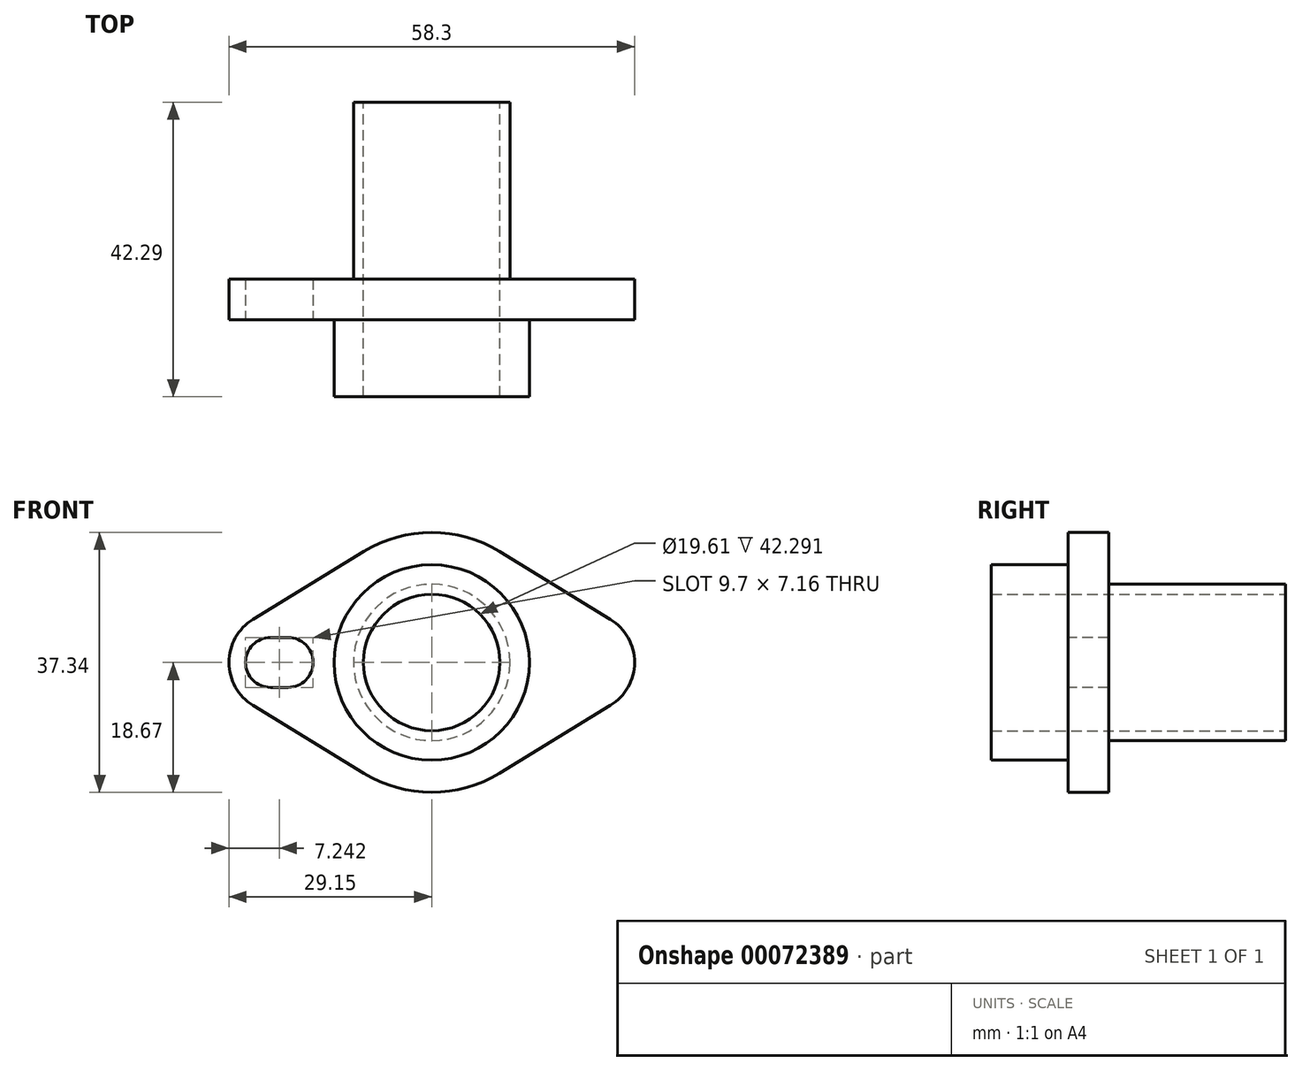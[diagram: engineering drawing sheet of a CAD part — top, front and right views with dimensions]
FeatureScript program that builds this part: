
annotation { "Feature Type Name" : "Feature", "Feature Type Description" : "" }
export const myFeature = defineFeature(function(context is Context, id is Id, definition is map)
    precondition{}
    {
        {
            var Q0;
            Q0=qCreatedBy(makeId("Front.planeOp"),FACE);
            var sketch = newSketch(context, id + "F0", { "sketchPlane" : qUnion([Q0])});
            skCircle(sketch, "E0", {"center": v(0, 0) * mm, "radius": 9.8 * mm});
            skArc(sketch, "E1", {"start": v(9.74, 15.93) * mm, "mid": v(0, 18.67) * mm, "end": v(-9.74, 15.93) * mm});
            skArc(sketch, "E2", {"start": v(25.68, -6.18) * mm, "mid": v(29.15, 0) * mm, "end": v(25.68, 6.18) * mm});
            skLineSegment(sketch, "E3", {"start": v(9.74, 15.93) * mm, "end": v(25.68, 6.18) * mm});
            skLineSegment(sketch, "E4", {"start": v(9.74, -15.93) * mm, "end": v(25.68, -6.18) * mm});
            skLineSegment(sketch, "E5.MirrorCS", {"start": v(-9.74, 15.93) * mm, "end": v(-25.68, 6.18) * mm});
            skLineSegment(sketch, "E6.MirrorCS", {"start": v(-9.74, -15.93) * mm, "end": v(-25.68, -6.18) * mm});
            skArc(sketch, "E7.MirrorCS", {"start": v(-25.68, -6.18) * mm, "mid": v(-29.15, 0) * mm, "end": v(-25.68, 6.18) * mm});
            skArc(sketch, "E8.trimOffspring", {"start": v(-9.74, -15.93) * mm, "mid": v(0, -18.67) * mm, "end": v(9.74, -15.93) * mm});
            skSolve(sketch);
        }
        {
            var Q0;
            Q0 = qSketchRegion(id + "F0", true);
            extrude(context, id + "F1", {"entities" : qUnion([Q0]), "depth" : 5.84 * mm});
        }
        {
            var Q0;
            Q0=makeQuery(id+"F1.opExtrude","CAP_FACE",FACE,{"disambiguationData":[OSD([sQuery(id+"F0.wireOp",EDGE,"E0"),sQuery(id+"F0.wireOp",EDGE,"E1"),sQuery(id+"F0.wireOp",EDGE,"E2"),sQuery(id+"F0.wireOp",EDGE,"E3"),sQuery(id+"F0.wireOp",EDGE,"E4"),sQuery(id+"F0.wireOp",EDGE,"E5.MirrorCS"),sQuery(id+"F0.wireOp",EDGE,"E6.MirrorCS"),sQuery(id+"F0.wireOp",EDGE,"E7.MirrorCS"),sQuery(id+"F0.wireOp",EDGE,"E8.trimOffspring")])],"isStart":false});
            var sketch = newSketch(context, id + "F2", { "sketchPlane" : qUnion([Q0])});
            skLineSegment(sketch, "E9", {"start": v(-23.18, 0) * mm, "end": v(-20.64, 0) * mm});
            skArc(sketch, "E10.0.startCap", {"start": v(-23.18, -3.58) * mm, "mid": v(-26.76, 0) * mm, "end": v(-23.18, 3.58) * mm});
            skArc(sketch, "E10.0.endCap", {"start": v(-20.64, 3.58) * mm, "mid": v(-17.06, 0) * mm, "end": v(-20.64, -3.58) * mm});
            skLineSegment(sketch, "E10.0.left", {"start": v(-23.18, 3.58) * mm, "end": v(-20.64, 3.58) * mm});
            skLineSegment(sketch, "E10.0.right", {"start": v(-23.18, -3.58) * mm, "end": v(-20.64, -3.58) * mm});
            skPoint(sketch, "E11", {"position": v(-21.9, 0) * mm});
            skSolve(sketch);
        }
        {
            var Q0;
            Q0 = qSketchRegion(id + "F2", true);
            extrude(context, id + "F3", {"entities" : qUnion([Q0]), "operationType" : NewBodyOperationType.REMOVE, "endBound" : BoundingType.THROUGH_ALL, "oppositeDirection" : true, "depth" : 25.4 * mm});
        }
        {
            var Q0;
            Q0=makeQuery(id+"F1.opExtrude","CAP_FACE",FACE,{"disambiguationData":[OSD([sQuery(id+"F0.wireOp",EDGE,"E0"),sQuery(id+"F0.wireOp",EDGE,"E1"),sQuery(id+"F0.wireOp",EDGE,"E2"),sQuery(id+"F0.wireOp",EDGE,"E3"),sQuery(id+"F0.wireOp",EDGE,"E4"),sQuery(id+"F0.wireOp",EDGE,"E5.MirrorCS"),sQuery(id+"F0.wireOp",EDGE,"E6.MirrorCS"),sQuery(id+"F0.wireOp",EDGE,"E7.MirrorCS"),sQuery(id+"F0.wireOp",EDGE,"E8.trimOffspring")])],"isStart":false});
            var sketch = newSketch(context, id + "F4", { "sketchPlane" : qUnion([Q0])});
            skCircle(sketch, "E12.0", {"center": v(0, 0) * mm, "radius": 9.8 * mm});
            skCircle(sketch, "E13", {"center": v(0, 0) * mm, "radius": 14.03 * mm});
            skSolve(sketch);
        }
        {
            var Q0;
            Q0 = qSketchRegion(id + "F4", true);
            extrude(context, id + "F5", {"entities" : qUnion([Q0]), "operationType" : NewBodyOperationType.ADD, "depth" : 11.05 * mm});
        }
        {
            var Q0;
            Q0=makeQuery(id+"F1.opExtrude","CAP_FACE",FACE,{"disambiguationData":[OSD([sQuery(id+"F0.wireOp",EDGE,"E0"),sQuery(id+"F0.wireOp",EDGE,"E1"),sQuery(id+"F0.wireOp",EDGE,"E2"),sQuery(id+"F0.wireOp",EDGE,"E3"),sQuery(id+"F0.wireOp",EDGE,"E4"),sQuery(id+"F0.wireOp",EDGE,"E5.MirrorCS"),sQuery(id+"F0.wireOp",EDGE,"E6.MirrorCS"),sQuery(id+"F0.wireOp",EDGE,"E7.MirrorCS"),sQuery(id+"F0.wireOp",EDGE,"E8.trimOffspring")])],"isStart":true});
            var sketch = newSketch(context, id + "F6", { "sketchPlane" : qUnion([Q0])});
            skCircle(sketch, "E14.0", {"center": v(0, 0) * mm, "radius": 9.8 * mm});
            skCircle(sketch, "E15", {"center": v(0, 0) * mm, "radius": 11.24 * mm});
            skSolve(sketch);
        }
        {
            var Q0;
            Q0 = qSketchRegion(id + "F6", true);
            extrude(context, id + "F7", {"entities" : qUnion([Q0]), "operationType" : NewBodyOperationType.ADD, "depth" : 25.4 * mm});
        }
    });
